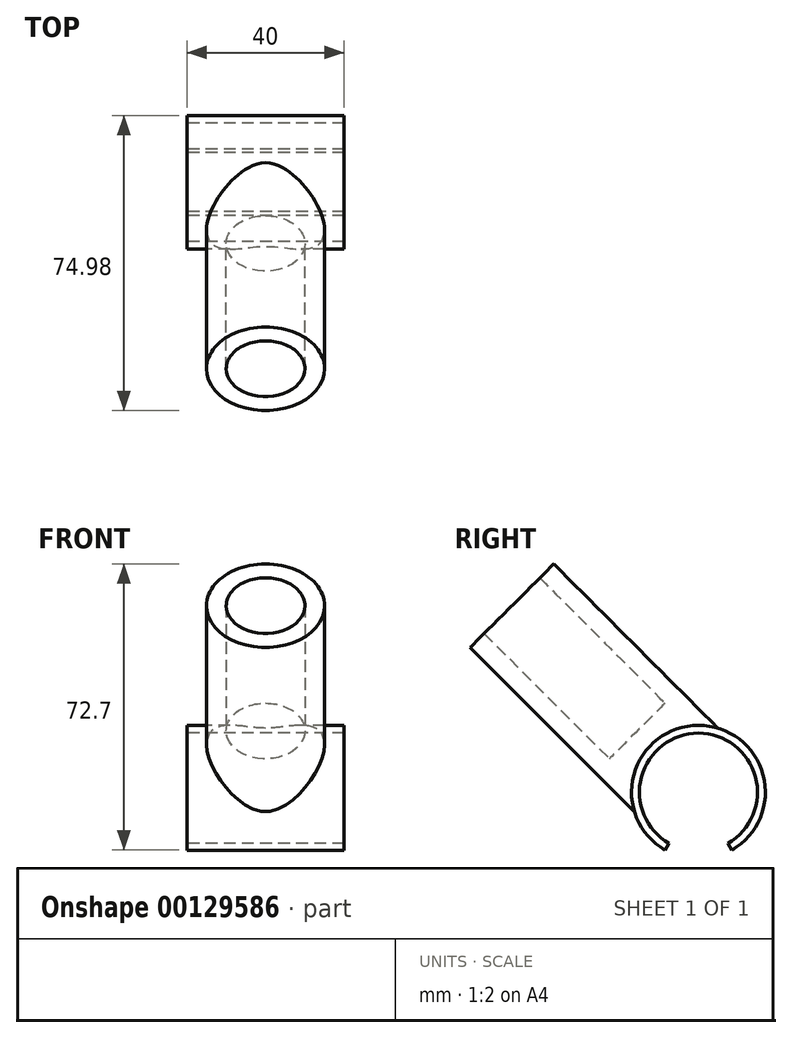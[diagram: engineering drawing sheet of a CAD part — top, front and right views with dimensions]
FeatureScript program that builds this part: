
annotation { "Feature Type Name" : "Feature", "Feature Type Description" : "" }
export const myFeature = defineFeature(function(context is Context, id is Id, definition is map)
    precondition{}
    {
        {
            var Q0;
            Q0=qCreatedBy(makeId("Right.planeOp"),FACE);
            var sketch = newSketch(context, id + "F0", { "sketchPlane" : qUnion([Q0])});
            skArc(sketch, "E0", {"start": v(7.5, -13) * mm, "mid": v(0, 15) * mm, "end": v(-7.5, -13) * mm});
            skArc(sketch, "E1.0", {"start": v(8.5, -14.72) * mm, "mid": v(0, 17) * mm, "end": v(-8.5, -14.72) * mm});
            skLineSegment(sketch, "E2", {"start": v(0, 0) * mm, "end": v(-7.5, -13) * mm, "construction": true});
            skLineSegment(sketch, "E3", {"start": v(-7.5, -13) * mm, "end": v(7.5, -13) * mm, "construction": true});
            skLineSegment(sketch, "E4", {"start": v(7.5, -13) * mm, "end": v(0, 0) * mm, "construction": true});
            skLineSegment(sketch, "E5", {"start": v(0, 0) * mm, "end": v(0, -13) * mm, "construction": true});
            skLineSegment(sketch, "E6", {"start": v(-7.5, -13) * mm, "end": v(-8.5, -14.72) * mm});
            skLineSegment(sketch, "E7", {"start": v(7.5, -13) * mm, "end": v(8.5, -14.72) * mm});
            skSolve(sketch);
        }
        {
            var Q0;
            Q0 = qSketchRegion(id + "F0", true);
            extrude(context, id + "F1", {"entities" : qUnion([Q0]), "endBound" : BoundingType.SYMMETRIC, "depth" : 40 * mm});
        }
        {
            var Q0;
            Q0=qCreatedBy(makeId("Right.planeOp"),FACE);
            var sketch = newSketch(context, id + "F2", { "sketchPlane" : qUnion([Q0])});
            skLineSegment(sketch, "E8", {"start": v(0, 0) * mm, "end": v(-10.6, 10.6) * mm, "construction": true});
            skArc(sketch, "E9.0", {"start": v(-10.6, 10.6) * mm, "mid": v(-15, 0) * mm, "end": v(-10.6, -10.6) * mm});
            skLineSegment(sketch, "E10", {"start": v(-10.6, 10.6) * mm, "end": v(-15.56, 15.56) * mm});
            skLineSegment(sketch, "E11", {"start": v(-15.56, 15.56) * mm, "end": v(-22.63, 8.49) * mm});
            skLineSegment(sketch, "E12", {"start": v(-22.63, 8.49) * mm, "end": v(-54.45, 40.3) * mm});
            skLineSegment(sketch, "E13", {"start": v(-54.45, 40.3) * mm, "end": v(-57.98, 36.77) * mm});
            skLineSegment(sketch, "E14", {"start": v(-57.98, 36.77) * mm, "end": v(-10.6, -10.6) * mm});
            skPoint(sketch, "E15.orphan", {"position": v(-7.5, -13) * mm});
            skPoint(sketch, "E16.orphan", {"position": v(7.5, -13) * mm});
            skSolve(sketch);
        }
        {
            var Q0;
            Q0 = qSketchRegion(id + "F2", true);
            var Q1;
            Q1=sQuery(id+"F2.wireOp",EDGE,"E8");
            revolve(context, id + "F3", {"operationType" : NewBodyOperationType.ADD, "entities" : qUnion([Q0]), "axis" : qUnion([Q1]), "revolveType" : RevolveType.FULL});
        }
        {
            var Q0;
            Q0=qCreatedBy(makeId("Right.planeOp"),FACE);
            var sketch = newSketch(context, id + "F4", { "sketchPlane" : qUnion([Q0])});
            skCircle(sketch, "E17", {"center": v(0, 0) * mm, "radius": 15 * mm});
            skSolve(sketch);
        }
        {
            var Q0;
            Q0 = qSketchRegion(id + "F4", true);
            extrude(context, id + "F5", {"entities" : qUnion([Q0]), "operationType" : NewBodyOperationType.REMOVE, "endBound" : BoundingType.SYMMETRIC, "oppositeDirection" : true, "depth" : 1000 * mm});
        }
    });
